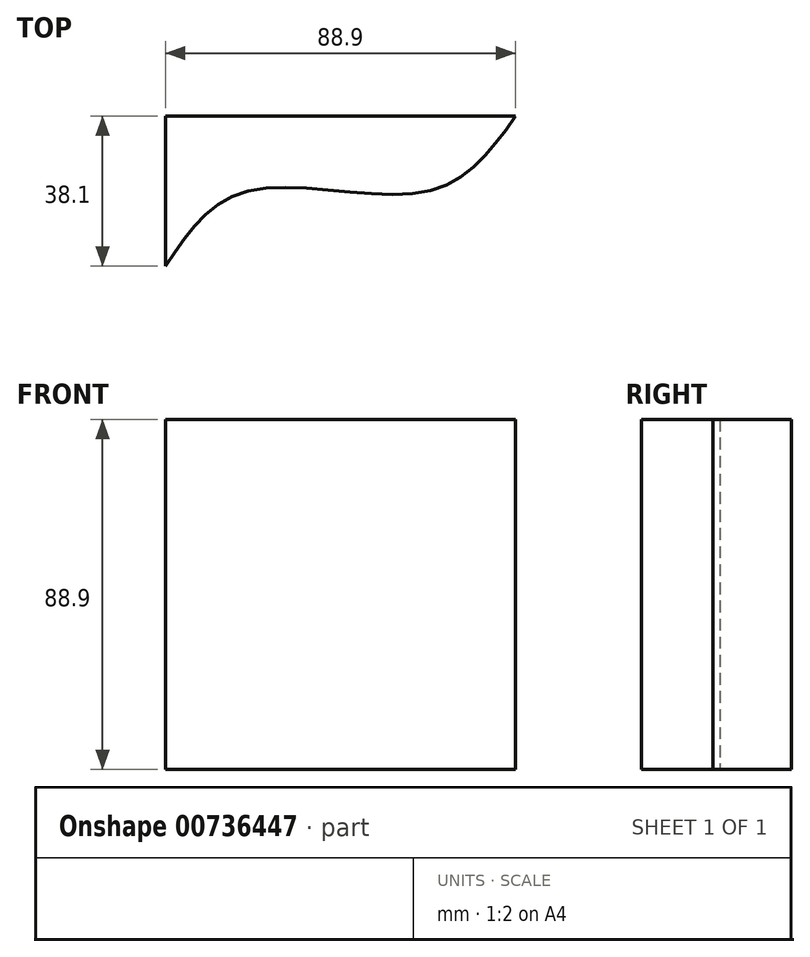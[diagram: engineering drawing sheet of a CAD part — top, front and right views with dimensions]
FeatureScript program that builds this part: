
annotation { "Feature Type Name" : "Feature", "Feature Type Description" : "" }
export const myFeature = defineFeature(function(context is Context, id is Id, definition is map)
    precondition{}
    {
        {
            var Q0;
            Q0=qCreatedBy(makeId("Top.planeOp"),FACE);
            var sketch = newSketch(context, id + "F0", { "sketchPlane" : qUnion([Q0])});
            skLineSegment(sketch, "E0.bottom", {"start": v(44.45, -19.05) * mm, "end": v(-44.45, -19.05) * mm});
            skLineSegment(sketch, "E0.top", {"start": v(44.45, 19.05) * mm, "end": v(-44.45, 19.05) * mm});
            skLineSegment(sketch, "E0.left", {"start": v(44.45, -19.05) * mm, "end": v(44.45, 19.05) * mm});
            skLineSegment(sketch, "E0.right", {"start": v(-44.45, -19.05) * mm, "end": v(-44.45, 19.05) * mm});
            skPoint(sketch, "E0.middle", {"position": v(0, 0) * mm});
            skFitSpline(sketch, "E1", {"points": [v(-44.45, -19.05) * mm, v(-23.54, 0) * mm, v(22.4, 0) * mm, v(44.45, 19.05) * mm], "startDerivative": vector(53.79, 81.7) * mm, "endDerivative": vector(56.77, 80.8) * mm});
            skSolve(sketch);
        }
        {
            var Q0;
            Q0=makeQuery(id+"F0.imprint","IMPRINT",FACE,{"disambiguationData":[TD([[makeQuery(id+"F0.imprint","IMPRINT",EDGE,{"derivedFrom":sQuery(id+"F0.wireOp",EDGE,"E0.top")}),1.0]])]});
            extrude(context, id + "F1", {"entities" : qUnion([Q0]), "depth" : 88.9 * mm, "offsetDistance" : 25.4 * mm});
        }
    });
